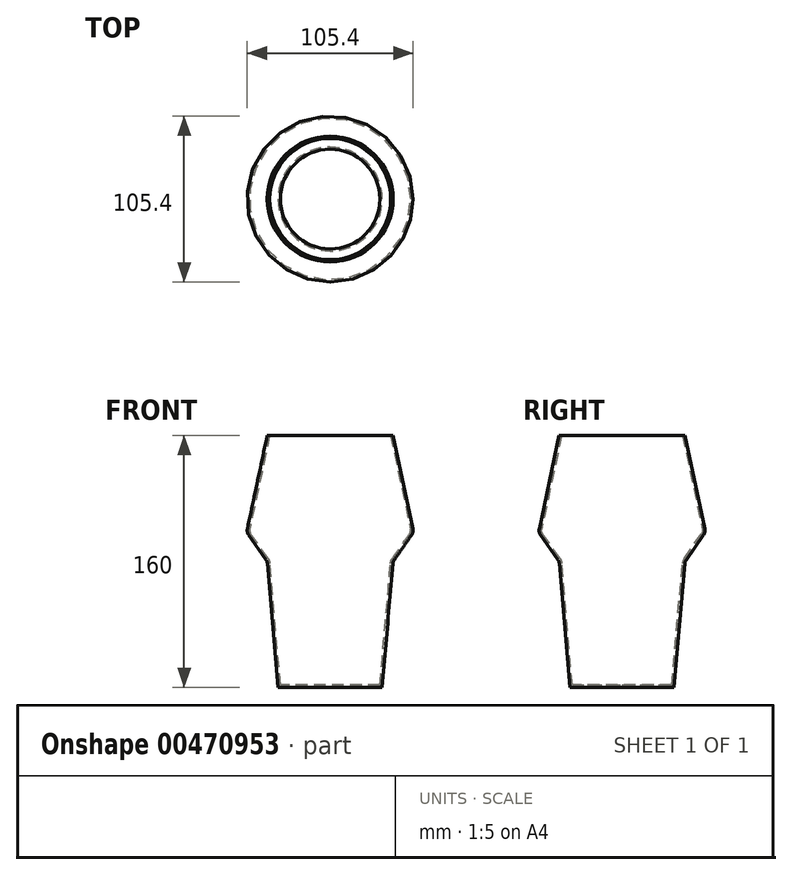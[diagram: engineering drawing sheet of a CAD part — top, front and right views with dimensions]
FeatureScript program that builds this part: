
annotation { "Feature Type Name" : "Feature", "Feature Type Description" : "" }
export const myFeature = defineFeature(function(context is Context, id is Id, definition is map)
    precondition{}
    {
        {
            var Q0;
            Q0=qCreatedBy(makeId("Front.planeOp"),FACE);
            var sketch = newSketch(context, id + "F0", { "sketchPlane" : qUnion([Q0])});
            skLineSegment(sketch, "E0", {"start": v(-33, 0) * mm, "end": v(0, 0) * mm});
            skLineSegment(sketch, "E1", {"start": v(0, 0) * mm, "end": v(0, 160) * mm});
            skLineSegment(sketch, "E2", {"start": v(0, 160) * mm, "end": v(-40, 160) * mm});
            skLineSegment(sketch, "E3", {"start": v(-40, 160) * mm, "end": v(-53.04, 98.63) * mm});
            skLineSegment(sketch, "E4", {"start": v(-53.04, 98.63) * mm, "end": v(-40, 80) * mm});
            skLineSegment(sketch, "E5", {"start": v(-40, 80) * mm, "end": v(-33, 0) * mm});
            skSolve(sketch);
        }
        {
            var Q0;
            Q0=makeQuery(id+"F0.imprint","IMPRINT",FACE,{"disambiguationData":[TD([[makeQuery(id+"F0.imprint","IMPRINT",EDGE,{"derivedFrom":sQuery(id+"F0.wireOp",EDGE,"E0")}),1.0]])]});
            var Q1;
            Q1 = qConstructionFilter(qBodyType(qCreatedBy(id + "F0" ,EDGE), BodyType.WIRE), ConstructionObject.NO);
            var Q2;
            Q2=sQuery(id+"F0.wireOp",EDGE,"E1");
            revolve(context, id + "F1", {"entities" : qUnion([Q0]), "surfaceEntities" : qUnion([Q1]), "axis" : qUnion([Q2]), "revolveType" : RevolveType.FULL});
        }
        {
            var Q0;
            Q0=makeQuery(id+"F1.opRevolve","SWEPT_EDGE",EDGE,{"disambiguationData":[OSD([sQuery(id+"F0.wireOp",EDGE,"E3"),sQuery(id+"F0.wireOp",EDGE,"E4")])]});
            var Q1;
            Q1=makeQuery(id+"F1.opRevolve","SWEPT_EDGE",EDGE,{"disambiguationData":[OSD([sQuery(id+"F0.wireOp",EDGE,"E4"),sQuery(id+"F0.wireOp",EDGE,"E5")])]});
            fillet(context, id + "F2", {"entities" : qUnion([Q0, Q1]), "radius" : 5 * mm, "tangentPropagation" : true, "allowEdgeOverflow" : false});
        }
        {
            var Q0;
            Q0=makeQuery(id+"F1.opRevolve","SWEPT_FACE",FACE,{"disambiguationData":[OSD([sQuery(id+"F0.wireOp",EDGE,"E2")])]});
            shell(context, id + "F3", {"entities" : qUnion([Q0]), "thickness" : 1.5 * mm});
        }
    });
